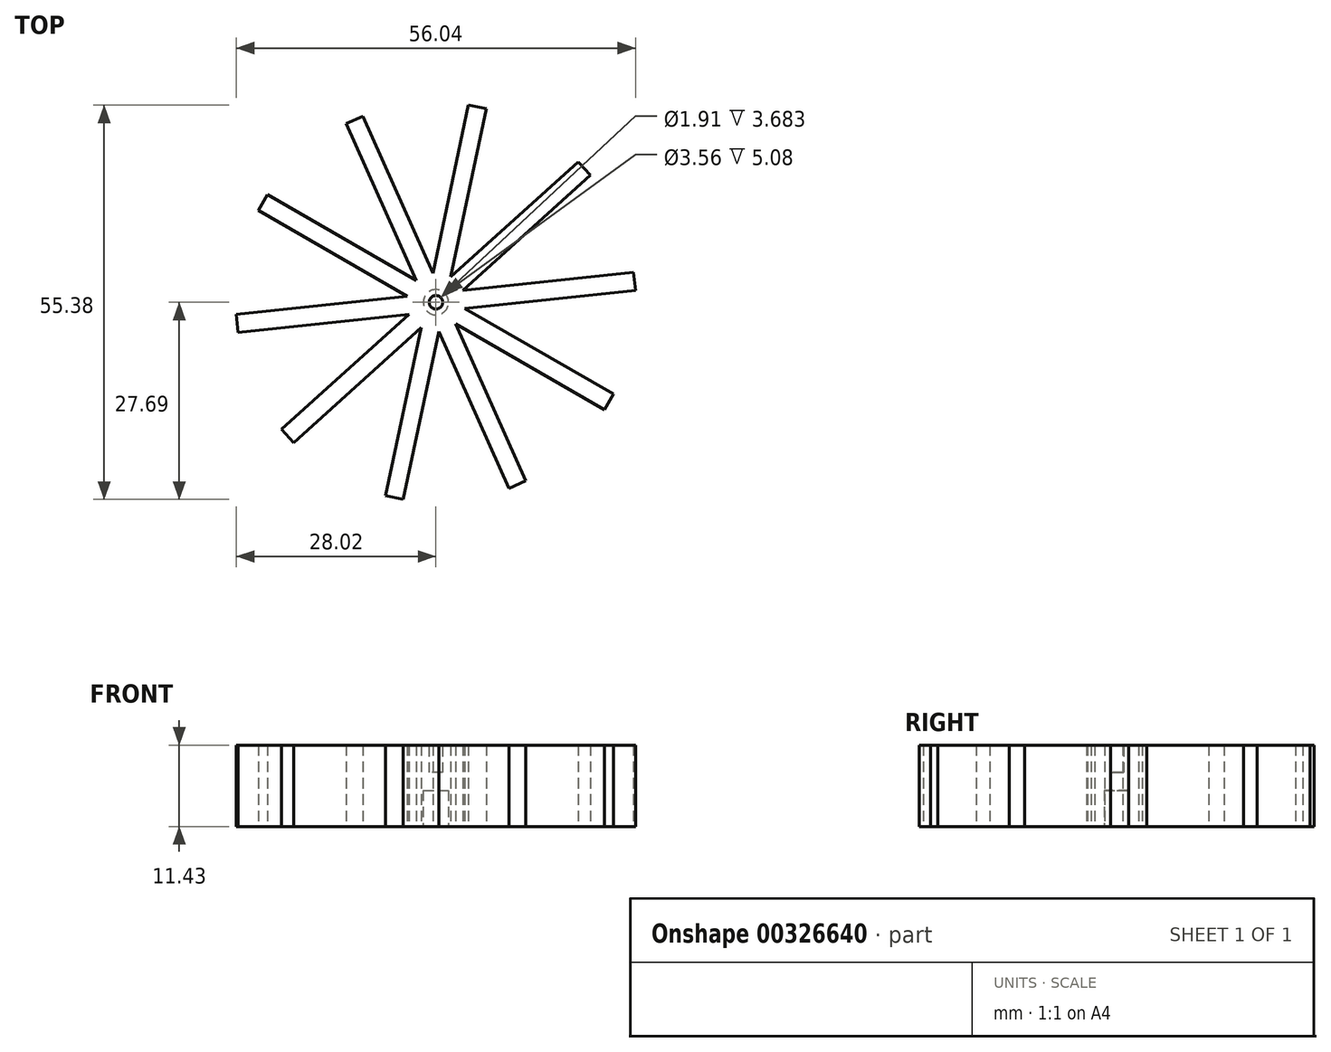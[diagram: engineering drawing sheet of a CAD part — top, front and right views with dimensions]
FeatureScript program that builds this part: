
annotation { "Feature Type Name" : "Feature", "Feature Type Description" : "" }
export const myFeature = defineFeature(function(context is Context, id is Id, definition is map)
    precondition{}
    {
        {
            var Q0;
            Q0=qCreatedBy(makeId("Top.planeOp"),FACE);
            var sketch = newSketch(context, id + "F0", { "sketchPlane" : qUnion([Q0])});
            skCircle(sketch, "E0", {"center": v(0, 0) * mm, "radius": 0.95 * mm});
            skCircle(sketch, "E1.cCircle", {"center": v(0, 0) * mm, "radius": 3.9 * mm, "construction": true});
            skLineSegment(sketch, "E1.0", {"start": v(2.75, -3.05) * mm, "end": v(0.43, -4.09) * mm});
            skLineSegment(sketch, "E1.1", {"start": v(0.43, -4.09) * mm, "end": v(-2.05, -3.56) * mm});
            skLineSegment(sketch, "E1.2", {"start": v(-2.05, -3.56) * mm, "end": v(-3.75, -1.67) * mm});
            skLineSegment(sketch, "E1.3", {"start": v(-3.75, -1.67) * mm, "end": v(-4.02, 0.85) * mm});
            skLineSegment(sketch, "E1.4", {"start": v(-4.02, 0.85) * mm, "end": v(-2.75, 3.05) * mm});
            skLineSegment(sketch, "E1.5", {"start": v(-2.75, 3.05) * mm, "end": v(-0.43, 4.09) * mm});
            skLineSegment(sketch, "E1.6", {"start": v(-0.43, 4.09) * mm, "end": v(2.05, 3.56) * mm});
            skLineSegment(sketch, "E1.7", {"start": v(2.05, 3.56) * mm, "end": v(3.75, 1.67) * mm});
            skLineSegment(sketch, "E1.8", {"start": v(3.75, 1.67) * mm, "end": v(4.02, -0.85) * mm});
            skLineSegment(sketch, "E1.9", {"start": v(4.02, -0.85) * mm, "end": v(2.75, -3.05) * mm});
            skPoint(sketch, "E1.0.midPoint", {"position": v(1.6, -3.57) * mm});
            skSolve(sketch);
        }
        {
            var Q0;
            Q0=makeQuery(id+"F0.imprint","IMPRINT",FACE,{"disambiguationData":[TD([[makeQuery(id+"F0.imprint","IMPRINT",EDGE,{"derivedFrom":sQuery(id+"F0.wireOp",EDGE,"E0")}),-1.0]])]});
            extrude(context, id + "F1", {"entities" : qUnion([Q0]), "depth" : 3.8 * mm});
        }
        {
            var Q0;
            Q0=makeQuery(id+"F1.opExtrude","CAP_EDGE",EDGE,{"disambiguationData":[OSD([sQuery(id+"F0.wireOp",EDGE,"E0")])],"isStart":false});
            fillet(context, id + "F2", {"entities" : qUnion([Q0]), "radius" : 0.13 * mm, "tangentPropagation" : true, "allowEdgeOverflow" : false});
        }
        {
            var Q0;
            Q0=makeQuery(id+"F0.imprint","IMPRINT",FACE,{"disambiguationData":[TD([[makeQuery(id+"F0.imprint","IMPRINT",EDGE,{"derivedFrom":sQuery(id+"F0.wireOp",EDGE,"E0")}),-1.0]])]});
            var Q1;
            Q1=makeQuery(id+"F0.imprint","IMPRINT",FACE,{"disambiguationData":[TD([[makeQuery(id+"F0.imprint","IMPRINT",EDGE,{"derivedFrom":sQuery(id+"F0.wireOp",EDGE,"E0")}),1.0]])]});
            extrude(context, id + "F3", {"entities" : qUnion([Q0, Q1]), "operationType" : NewBodyOperationType.ADD, "oppositeDirection" : true, "depth" : 2.54 * mm});
        }
        {
            var Q0;
            {var subQ0=sQuery(id+"F0.wireOp",EDGE,"E1.7");Q0=makeQuery(id+"F3.boolean.opBoolean","MERGE",FACE,{"derivedFrom":[makeQuery(id+"F1.opExtrude","SWEPT_FACE",FACE,{"disambiguationData":[OSD([subQ0])]}),makeQuery(id+"F3.opExtrude","SWEPT_FACE",FACE,{"disambiguationData":[OSD([subQ0])]})]});}
            extrude(context, id + "F4", {"entities" : qUnion([Q0]), "operationType" : NewBodyOperationType.ADD, "depth" : 24.13 * mm});
        }
        {
            var Q0;
            {var subQ0=sQuery(id+"F0.wireOp",EDGE,"E1.8");Q0=makeQuery(id+"F3.boolean.opBoolean","MERGE",FACE,{"derivedFrom":[makeQuery(id+"F1.opExtrude","SWEPT_FACE",FACE,{"disambiguationData":[OSD([subQ0])]}),makeQuery(id+"F3.opExtrude","SWEPT_FACE",FACE,{"disambiguationData":[OSD([subQ0])]})]});}
            extrude(context, id + "F5", {"entities" : qUnion([Q0]), "operationType" : NewBodyOperationType.ADD, "depth" : 24.13 * mm});
        }
        {
            var Q0;
            {var subQ0=sQuery(id+"F0.wireOp",EDGE,"E1.9");Q0=makeQuery(id+"F3.boolean.opBoolean","MERGE",FACE,{"derivedFrom":[makeQuery(id+"F1.opExtrude","SWEPT_FACE",FACE,{"disambiguationData":[OSD([subQ0])]}),makeQuery(id+"F3.opExtrude","SWEPT_FACE",FACE,{"disambiguationData":[OSD([subQ0])]})]});}
            extrude(context, id + "F6", {"entities" : qUnion([Q0]), "operationType" : NewBodyOperationType.ADD, "depth" : 24.13 * mm});
        }
        {
            var Q0;
            {var subQ0=sQuery(id+"F0.wireOp",EDGE,"E1.0");Q0=makeQuery(id+"F3.boolean.opBoolean","MERGE",FACE,{"derivedFrom":[makeQuery(id+"F1.opExtrude","SWEPT_FACE",FACE,{"disambiguationData":[OSD([subQ0])]}),makeQuery(id+"F3.opExtrude","SWEPT_FACE",FACE,{"disambiguationData":[OSD([subQ0])]})]});}
            extrude(context, id + "F7", {"entities" : qUnion([Q0]), "operationType" : NewBodyOperationType.ADD, "depth" : 24.13 * mm});
        }
        {
            var Q0;
            {var subQ0=sQuery(id+"F0.wireOp",EDGE,"E1.1");Q0=makeQuery(id+"F3.boolean.opBoolean","MERGE",FACE,{"derivedFrom":[makeQuery(id+"F1.opExtrude","SWEPT_FACE",FACE,{"disambiguationData":[OSD([subQ0])]}),makeQuery(id+"F3.opExtrude","SWEPT_FACE",FACE,{"disambiguationData":[OSD([subQ0])]})]});}
            extrude(context, id + "F8", {"entities" : qUnion([Q0]), "operationType" : NewBodyOperationType.ADD, "depth" : 24.13 * mm});
        }
        {
            var Q0;
            {var subQ0=sQuery(id+"F0.wireOp",EDGE,"E1.2");Q0=makeQuery(id+"F3.boolean.opBoolean","MERGE",FACE,{"derivedFrom":[makeQuery(id+"F1.opExtrude","SWEPT_FACE",FACE,{"disambiguationData":[OSD([subQ0])]}),makeQuery(id+"F3.opExtrude","SWEPT_FACE",FACE,{"disambiguationData":[OSD([subQ0])]})]});}
            extrude(context, id + "F9", {"entities" : qUnion([Q0]), "operationType" : NewBodyOperationType.ADD, "depth" : 24.13 * mm});
        }
        {
            var Q0;
            {var subQ0=sQuery(id+"F0.wireOp",EDGE,"E1.3");Q0=makeQuery(id+"F3.boolean.opBoolean","MERGE",FACE,{"derivedFrom":[makeQuery(id+"F1.opExtrude","SWEPT_FACE",FACE,{"disambiguationData":[OSD([subQ0])]}),makeQuery(id+"F3.opExtrude","SWEPT_FACE",FACE,{"disambiguationData":[OSD([subQ0])]})]});}
            extrude(context, id + "F10", {"entities" : qUnion([Q0]), "operationType" : NewBodyOperationType.ADD, "depth" : 24.13 * mm});
        }
        {
            var Q0;
            {var subQ0=sQuery(id+"F0.wireOp",EDGE,"E1.4");Q0=makeQuery(id+"F3.boolean.opBoolean","MERGE",FACE,{"derivedFrom":[makeQuery(id+"F1.opExtrude","SWEPT_FACE",FACE,{"disambiguationData":[OSD([subQ0])]}),makeQuery(id+"F3.opExtrude","SWEPT_FACE",FACE,{"disambiguationData":[OSD([subQ0])]})]});}
            extrude(context, id + "F11", {"entities" : qUnion([Q0]), "operationType" : NewBodyOperationType.ADD, "depth" : 24.13 * mm});
        }
        {
            var Q0;
            {var subQ0=sQuery(id+"F0.wireOp",EDGE,"E1.5");Q0=makeQuery(id+"F3.boolean.opBoolean","MERGE",FACE,{"derivedFrom":[makeQuery(id+"F1.opExtrude","SWEPT_FACE",FACE,{"disambiguationData":[OSD([subQ0])]}),makeQuery(id+"F3.opExtrude","SWEPT_FACE",FACE,{"disambiguationData":[OSD([subQ0])]})]});}
            extrude(context, id + "F12", {"entities" : qUnion([Q0]), "operationType" : NewBodyOperationType.ADD, "depth" : 24.13 * mm});
        }
        {
            var Q0;
            {var subQ0=sQuery(id+"F0.wireOp",EDGE,"E1.6");Q0=makeQuery(id+"F3.boolean.opBoolean","MERGE",FACE,{"derivedFrom":[makeQuery(id+"F1.opExtrude","SWEPT_FACE",FACE,{"disambiguationData":[OSD([subQ0])]}),makeQuery(id+"F3.opExtrude","SWEPT_FACE",FACE,{"disambiguationData":[OSD([subQ0])]})]});}
            extrude(context, id + "F13", {"entities" : qUnion([Q0]), "operationType" : NewBodyOperationType.ADD, "depth" : 24.13 * mm});
        }
        {
            var Q0;
            {var subQ0=sQuery(id+"F0.wireOp",EDGE,"E1.6");var subQ1=sQuery(id+"F0.wireOp",EDGE,"E1.5");var subQ2=sQuery(id+"F0.wireOp",EDGE,"E1.4");var subQ3=sQuery(id+"F0.wireOp",EDGE,"E1.3");var subQ4=sQuery(id+"F0.wireOp",EDGE,"E1.2");var subQ5=sQuery(id+"F0.wireOp",EDGE,"E1.1");var subQ6=sQuery(id+"F0.wireOp",EDGE,"E1.0");var subQ7=sQuery(id+"F0.wireOp",EDGE,"E1.9");var subQ8=sQuery(id+"F0.wireOp",EDGE,"E1.8");var subQ9=sQuery(id+"F0.wireOp",EDGE,"E1.7");Q0=makeQuery(id+"F13.boolean.opBoolean","MERGE",FACE,{"derivedFrom":[makeQuery(id+"F12.boolean.opBoolean","MERGE",FACE,{"derivedFrom":[makeQuery(id+"F11.boolean.opBoolean","MERGE",FACE,{"derivedFrom":[makeQuery(id+"F10.boolean.opBoolean","MERGE",FACE,{"derivedFrom":[makeQuery(id+"F9.boolean.opBoolean","MERGE",FACE,{"derivedFrom":[makeQuery(id+"F8.boolean.opBoolean","MERGE",FACE,{"derivedFrom":[makeQuery(id+"F7.boolean.opBoolean","MERGE",FACE,{"derivedFrom":[makeQuery(id+"F6.boolean.opBoolean","MERGE",FACE,{"derivedFrom":[makeQuery(id+"F5.boolean.opBoolean","MERGE",FACE,{"derivedFrom":[makeQuery(id+"F4.boolean.opBoolean","MERGE",FACE,{"derivedFrom":[makeQuery(id+"F3.opExtrude","CAP_FACE",FACE,{"disambiguationData":[OSD([subQ6,subQ5,subQ4,subQ3,subQ2,subQ1,subQ0,subQ9,subQ8,subQ7])],"isStart":false}),makeQuery(id+"F4.opExtrude","SWEPT_FACE",FACE,{"disambiguationData":[OSD([subQ9]),TDD([makeQuery(id+"F3.opExtrude","CAP_EDGE",EDGE,{"disambiguationData":[OSD([subQ9])],"isStart":false})])]})]}),makeQuery(id+"F5.opExtrude","SWEPT_FACE",FACE,{"disambiguationData":[OSD([subQ8]),TDD([makeQuery(id+"F3.opExtrude","CAP_EDGE",EDGE,{"disambiguationData":[OSD([subQ8])],"isStart":false})])]})]}),makeQuery(id+"F6.opExtrude","SWEPT_FACE",FACE,{"disambiguationData":[OSD([subQ7]),TDD([makeQuery(id+"F3.opExtrude","CAP_EDGE",EDGE,{"disambiguationData":[OSD([subQ7])],"isStart":false})])]})]}),makeQuery(id+"F7.opExtrude","SWEPT_FACE",FACE,{"disambiguationData":[OSD([subQ6]),TDD([makeQuery(id+"F3.opExtrude","CAP_EDGE",EDGE,{"disambiguationData":[OSD([subQ6])],"isStart":false})])]})]}),makeQuery(id+"F8.opExtrude","SWEPT_FACE",FACE,{"disambiguationData":[OSD([subQ5]),TDD([makeQuery(id+"F3.opExtrude","CAP_EDGE",EDGE,{"disambiguationData":[OSD([subQ5])],"isStart":false})])]})]}),makeQuery(id+"F9.opExtrude","SWEPT_FACE",FACE,{"disambiguationData":[OSD([subQ4]),TDD([makeQuery(id+"F3.opExtrude","CAP_EDGE",EDGE,{"disambiguationData":[OSD([subQ4])],"isStart":false})])]})]}),makeQuery(id+"F10.opExtrude","SWEPT_FACE",FACE,{"disambiguationData":[OSD([subQ3]),TDD([makeQuery(id+"F3.opExtrude","CAP_EDGE",EDGE,{"disambiguationData":[OSD([subQ3])],"isStart":false})])]})]}),makeQuery(id+"F11.opExtrude","SWEPT_FACE",FACE,{"disambiguationData":[OSD([subQ2]),TDD([makeQuery(id+"F3.opExtrude","CAP_EDGE",EDGE,{"disambiguationData":[OSD([subQ2])],"isStart":false})])]})]}),makeQuery(id+"F12.opExtrude","SWEPT_FACE",FACE,{"disambiguationData":[OSD([subQ1]),TDD([makeQuery(id+"F3.opExtrude","CAP_EDGE",EDGE,{"disambiguationData":[OSD([subQ1])],"isStart":false})])]})]}),makeQuery(id+"F13.opExtrude","SWEPT_FACE",FACE,{"disambiguationData":[OSD([subQ0]),TDD([makeQuery(id+"F3.opExtrude","CAP_EDGE",EDGE,{"disambiguationData":[OSD([subQ0])],"isStart":false})])]})]});}
            extrude(context, id + "F14", {"entities" : qUnion([Q0]), "operationType" : NewBodyOperationType.ADD, "depth" : 5.08 * mm});
        }
        {
            var Q0;
            Q0=makeQuery(id+"F14.opExtrude","CAP_FACE",FACE,{"disambiguationData":[OSD([sQuery(id+"F0.wireOp",EDGE,"E1.0"),sQuery(id+"F0.wireOp",EDGE,"E1.1"),sQuery(id+"F0.wireOp",EDGE,"E1.2"),sQuery(id+"F0.wireOp",EDGE,"E1.3"),sQuery(id+"F0.wireOp",EDGE,"E1.4"),sQuery(id+"F0.wireOp",EDGE,"E1.5"),sQuery(id+"F0.wireOp",EDGE,"E1.6"),sQuery(id+"F0.wireOp",EDGE,"E1.7"),sQuery(id+"F0.wireOp",EDGE,"E1.8"),sQuery(id+"F0.wireOp",EDGE,"E1.9")])],"isStart":false});
            var sketch = newSketch(context, id + "F15", { "sketchPlane" : qUnion([Q0])});
            skCircle(sketch, "E2", {"center": v(0, 0) * mm, "radius": 1.78 * mm});
            skSolve(sketch);
        }
        {
            var Q0;
            Q0 = qSketchRegion(id + "F15", true);
            extrude(context, id + "F16", {"entities" : qUnion([Q0]), "operationType" : NewBodyOperationType.REMOVE, "oppositeDirection" : true, "depth" : 5.08 * mm});
        }
    });
